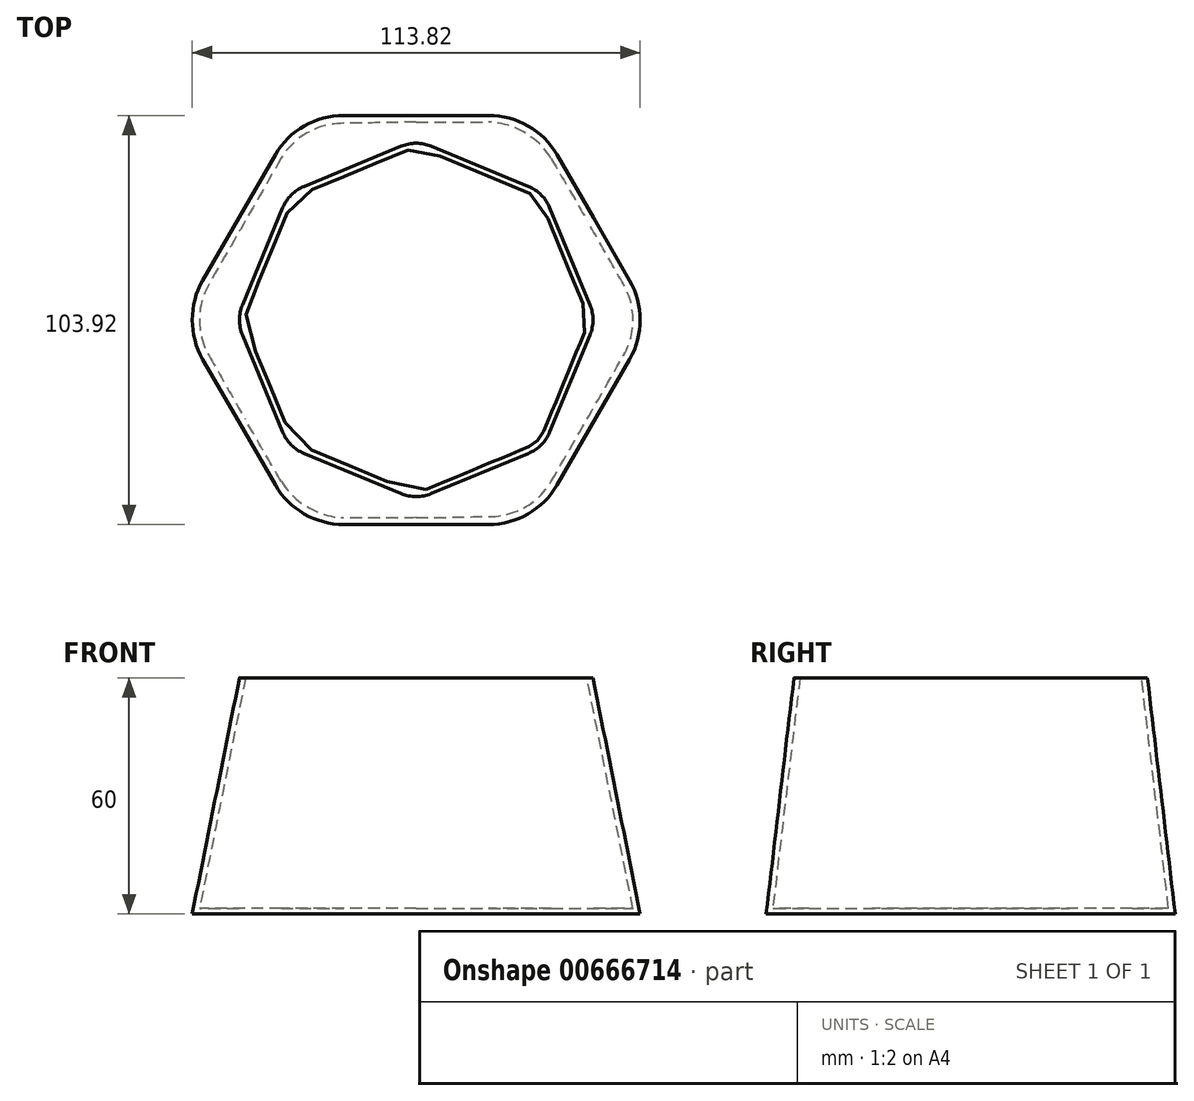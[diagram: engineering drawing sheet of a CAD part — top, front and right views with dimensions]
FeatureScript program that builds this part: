
annotation { "Feature Type Name" : "Feature", "Feature Type Description" : "" }
export const myFeature = defineFeature(function(context is Context, id is Id, definition is map)
    precondition{}
    {
        {
            var Q0;
            Q0=qCreatedBy(makeId("Top.planeOp"),FACE);
            var sketch = newSketch(context, id + "F0", { "sketchPlane" : qUnion([Q0])});
            skCircle(sketch, "E0.cCircle", {"center": v(0, 0) * mm, "radius": 60 * mm, "construction": true});
            skLineSegment(sketch, "E0.0", {"start": v(54.23, -10) * mm, "end": v(35.77, -41.96) * mm});
            skLineSegment(sketch, "E0.1", {"start": v(18.45, -51.96) * mm, "end": v(-18.45, -51.96) * mm});
            skLineSegment(sketch, "E0.2", {"start": v(-35.77, -41.96) * mm, "end": v(-54.23, -10) * mm});
            skLineSegment(sketch, "E0.3", {"start": v(-54.23, 10) * mm, "end": v(-35.77, 41.96) * mm});
            skLineSegment(sketch, "E0.4", {"start": v(-18.45, 51.96) * mm, "end": v(18.45, 51.96) * mm});
            skLineSegment(sketch, "E0.5", {"start": v(35.77, 41.96) * mm, "end": v(54.23, 10) * mm});
            skPoint(sketch, "E1.visualSharp", {"position": v(-30, 51.96) * mm});
            skArc(sketch, "E1.filletArc", {"start": v(-18.45, 51.96) * mm, "mid": v(-28.45, 49.28) * mm, "end": v(-35.77, 41.96) * mm});
            skPoint(sketch, "E2.visualSharp", {"position": v(30, 51.96) * mm});
            skArc(sketch, "E2.filletArc", {"start": v(35.77, 41.96) * mm, "mid": v(28.45, 49.28) * mm, "end": v(18.45, 51.96) * mm});
            skPoint(sketch, "E3.visualSharp", {"position": v(60, 0) * mm});
            skArc(sketch, "E3.filletArc", {"start": v(54.23, -10) * mm, "mid": v(56.9, 0) * mm, "end": v(54.23, 10) * mm});
            skPoint(sketch, "E4.visualSharp", {"position": v(30, -51.96) * mm});
            skArc(sketch, "E4.filletArc", {"start": v(18.45, -51.96) * mm, "mid": v(28.45, -49.28) * mm, "end": v(35.77, -41.96) * mm});
            skPoint(sketch, "E5.visualSharp", {"position": v(-30, -51.96) * mm});
            skArc(sketch, "E5.filletArc", {"start": v(-35.77, -41.96) * mm, "mid": v(-28.45, -49.28) * mm, "end": v(-18.45, -51.96) * mm});
            skPoint(sketch, "E6.visualSharp", {"position": v(-60, 0) * mm});
            skArc(sketch, "E6.filletArc", {"start": v(-54.23, 10) * mm, "mid": v(-56.9, 0) * mm, "end": v(-54.23, -10) * mm});
            skSolve(sketch);
        }
        {
            var Q0;
            Q0=qCreatedBy(makeId("Top.planeOp"),FACE);
            cPlane(context, id + "F1", {"entities" : qUnion([Q0]), "cplaneType" : CPlaneType.OFFSET, "offset" : 60 * mm, "width" : 150 * mm, "height" : 150 * mm});
        }
        {
            var Q0;
            Q0=qCreatedBy(id+"F1.planeOp",FACE);
            var sketch = newSketch(context, id + "F2", { "sketchPlane" : qUnion([Q0])});
            skCircle(sketch, "E7.cCircle", {"center": v(0, 0) * mm, "radius": 45.73 * mm, "construction": true});
            skLineSegment(sketch, "E7.0", {"start": v(-28.5, 33.92) * mm, "end": v(-3.83, 44.14) * mm});
            skLineSegment(sketch, "E7.1", {"start": v(3.83, 44.14) * mm, "end": v(28.5, 33.92) * mm});
            skLineSegment(sketch, "E7.2", {"start": v(33.92, 28.5) * mm, "end": v(44.14, 3.83) * mm});
            skLineSegment(sketch, "E7.3", {"start": v(44.14, -3.83) * mm, "end": v(33.92, -28.5) * mm});
            skLineSegment(sketch, "E7.4", {"start": v(28.5, -33.92) * mm, "end": v(3.83, -44.14) * mm});
            skLineSegment(sketch, "E7.5", {"start": v(-3.83, -44.14) * mm, "end": v(-28.5, -33.92) * mm});
            skLineSegment(sketch, "E7.6", {"start": v(-33.92, -28.5) * mm, "end": v(-44.14, -3.83) * mm});
            skLineSegment(sketch, "E7.7", {"start": v(-44.14, 3.83) * mm, "end": v(-33.92, 28.5) * mm});
            skPoint(sketch, "E8.visualSharp", {"position": v(-32.34, 32.34) * mm});
            skArc(sketch, "E8.filletArc", {"start": v(-28.5, 33.92) * mm, "mid": v(-31.75, 31.75) * mm, "end": v(-33.92, 28.5) * mm});
            skPoint(sketch, "E9.visualSharp", {"position": v(-45.73, 0) * mm});
            skArc(sketch, "E9.filletArc", {"start": v(-44.14, 3.83) * mm, "mid": v(-44.9, 0) * mm, "end": v(-44.14, -3.83) * mm});
            skPoint(sketch, "E10.visualSharp", {"position": v(-32.34, -32.34) * mm});
            skArc(sketch, "E10.filletArc", {"start": v(-33.92, -28.5) * mm, "mid": v(-31.75, -31.75) * mm, "end": v(-28.5, -33.92) * mm});
            skPoint(sketch, "E11.visualSharp", {"position": v(0, -45.73) * mm});
            skArc(sketch, "E11.filletArc", {"start": v(-3.83, -44.14) * mm, "mid": v(0, -44.9) * mm, "end": v(3.83, -44.14) * mm});
            skPoint(sketch, "E12.visualSharp", {"position": v(32.34, -32.34) * mm});
            skArc(sketch, "E12.filletArc", {"start": v(28.5, -33.92) * mm, "mid": v(31.75, -31.75) * mm, "end": v(33.92, -28.5) * mm});
            skPoint(sketch, "E13.visualSharp", {"position": v(45.73, 0) * mm});
            skArc(sketch, "E13.filletArc", {"start": v(44.14, -3.83) * mm, "mid": v(44.9, 0) * mm, "end": v(44.14, 3.83) * mm});
            skPoint(sketch, "E14.visualSharp", {"position": v(32.34, 32.34) * mm});
            skArc(sketch, "E14.filletArc", {"start": v(33.92, 28.5) * mm, "mid": v(31.75, 31.75) * mm, "end": v(28.5, 33.92) * mm});
            skPoint(sketch, "E15.visualSharp", {"position": v(0, 45.73) * mm});
            skArc(sketch, "E15.filletArc", {"start": v(3.83, 44.14) * mm, "mid": v(0, 44.9) * mm, "end": v(-3.83, 44.14) * mm});
            skSolve(sketch);
        }
        {
            var Q0;
            Q0 = qSketchRegion(id + "F0", true);
            var Q1;
            Q1 = qSketchRegion(id + "F2", true);
            loft(context, id + "F3", {"sheetProfilesArray" : [{ "sheetProfileEntities" : qUnion([Q0]) }, { "sheetProfileEntities" : qUnion([Q1]) }]});
        }
        {
            var Q0;
            Q0=makeQuery(id+"F3.opLoft","CAP_FACE",FACE,{"disambiguationData":[OSD([makeQuery(id+"F2.imprint","IMPRINT",FACE,{"disambiguationData":[TD([[makeQuery(id+"F2.imprint","IMPRINT",EDGE,{"derivedFrom":sQuery(id+"F2.wireOp",EDGE,"E7.0")}),-1.0]])]})])],"isStart":true});
            shell(context, id + "F4", {"entities" : qUnion([Q0]), "thickness" : 1.5 * mm});
        }
    });
